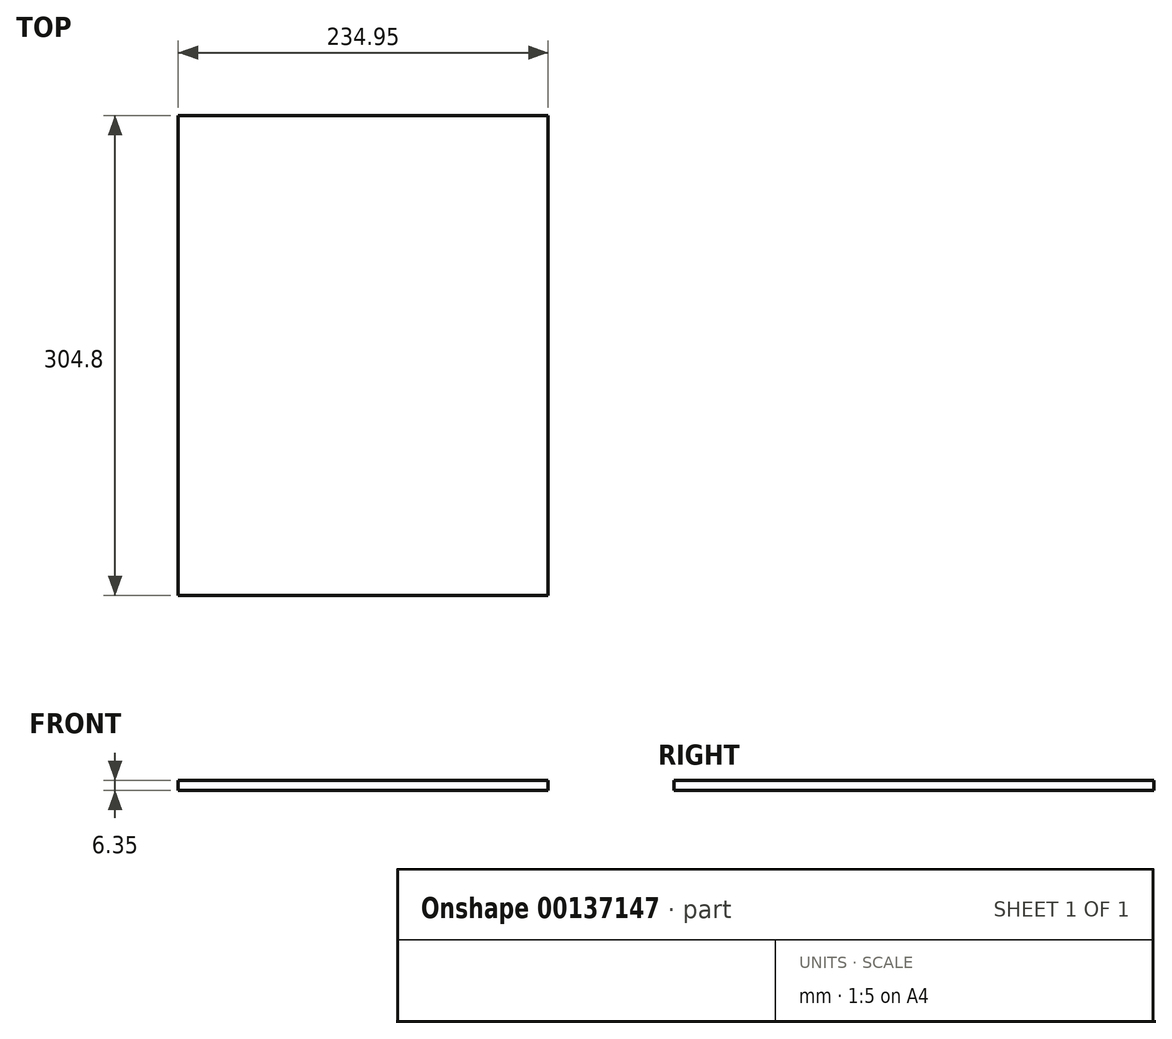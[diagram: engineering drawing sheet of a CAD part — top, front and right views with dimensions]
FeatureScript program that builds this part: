
annotation { "Feature Type Name" : "Feature", "Feature Type Description" : "" }
export const myFeature = defineFeature(function(context is Context, id is Id, definition is map)
    precondition{}
    {
        {
            var Q0;
            Q0=qCreatedBy(makeId("Top.planeOp"),FACE);
            var sketch = newSketch(context, id + "F0", { "sketchPlane" : qUnion([Q0])});
            skLineSegment(sketch, "E0.bottom", {"start": v(0, 0) * mm, "end": v(234.95, 0) * mm});
            skLineSegment(sketch, "E0.top", {"start": v(0, 304.8) * mm, "end": v(234.95, 304.8) * mm});
            skLineSegment(sketch, "E0.left", {"start": v(0, 0) * mm, "end": v(0, 304.8) * mm});
            skLineSegment(sketch, "E0.right", {"start": v(234.95, 0) * mm, "end": v(234.95, 304.8) * mm});
            skSolve(sketch);
        }
        {
            var Q0;
            Q0=makeQuery(id+"F0.imprint","IMPRINT",FACE,{"disambiguationData":[TD([[makeQuery(id+"F0.imprint","IMPRINT",EDGE,{"derivedFrom":sQuery(id+"F0.wireOp",EDGE,"E0.bottom")}),1.0]])]});
            extrude(context, id + "F1", {"entities" : qUnion([Q0]), "depth" : 6.35 * mm});
        }
    });
